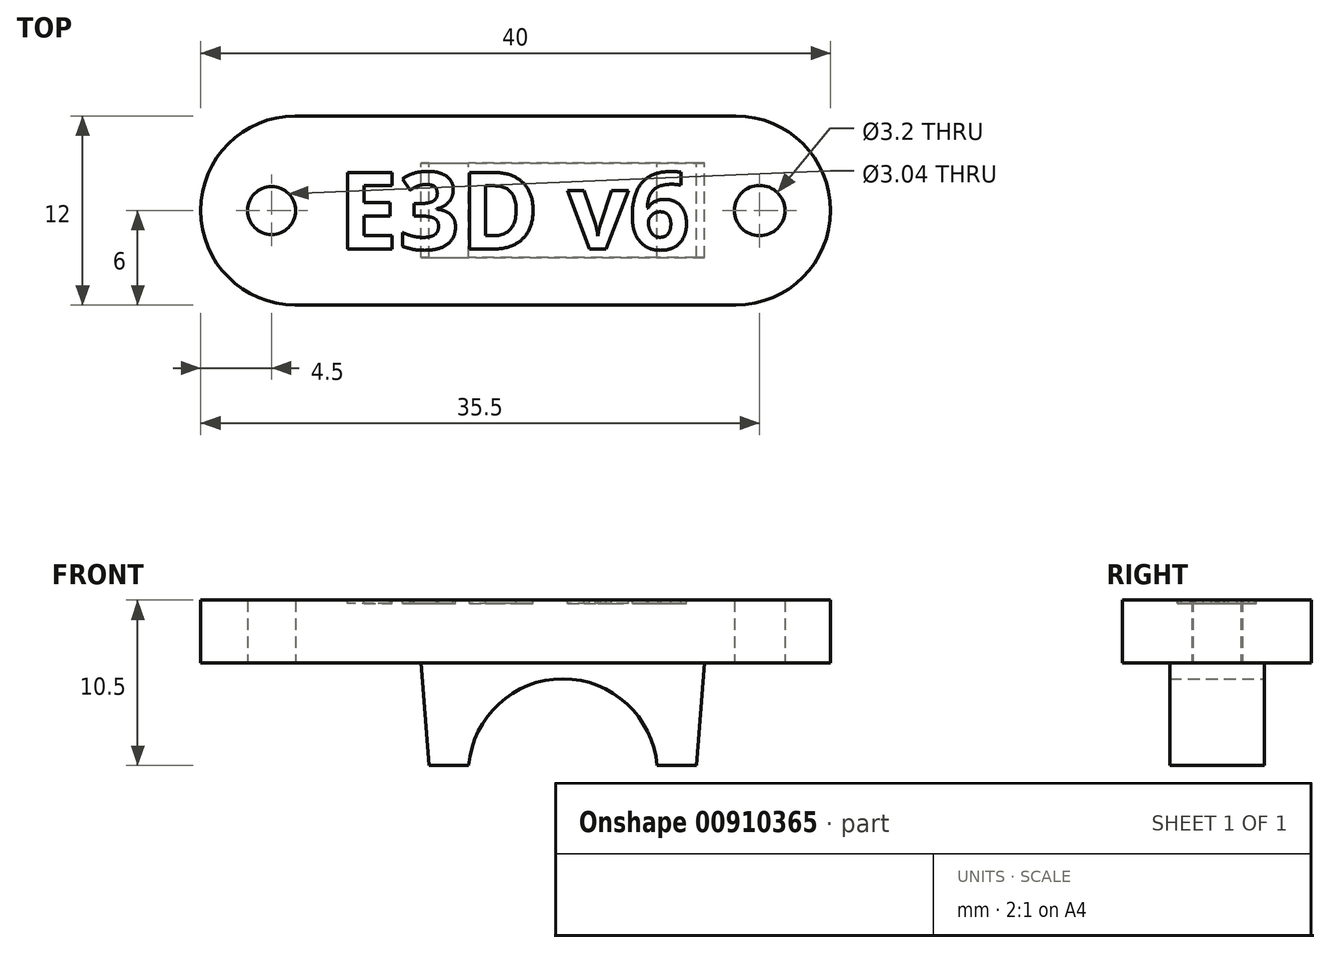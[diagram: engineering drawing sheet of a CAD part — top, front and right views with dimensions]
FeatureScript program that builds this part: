
annotation { "Feature Type Name" : "Feature", "Feature Type Description" : "" }
export const myFeature = defineFeature(function(context is Context, id is Id, definition is map)
    precondition{}
    {
        {
            var Q0;
            Q0=qCreatedBy(makeId("Top.planeOp"),FACE);
            var sketch = newSketch(context, id + "F0", { "sketchPlane" : qUnion([Q0])});
            skLineSegment(sketch, "E0.bottom", {"start": v(20, 6) * mm, "end": v(-20, 6) * mm});
            skLineSegment(sketch, "E0.top", {"start": v(20, -6) * mm, "end": v(-20, -6) * mm});
            skLineSegment(sketch, "E0.left", {"start": v(20, 6) * mm, "end": v(20, -6) * mm});
            skLineSegment(sketch, "E0.right", {"start": v(-20, 6) * mm, "end": v(-20, -6) * mm});
            skPoint(sketch, "E0.middle", {"position": v(0, 0) * mm});
            skCircle(sketch, "E1", {"center": v(15.5, 0) * mm, "radius": 1.6 * mm});
            skCircle(sketch, "E2", {"center": v(-15.5, 0) * mm, "radius": 1.52 * mm});
            skLineSegment(sketch, "E3", {"start": v(-15.5, 0) * mm, "end": v(15.5, 0) * mm, "construction": true});
            skSolve(sketch);
        }
        {
            var Q0;
            Q0 = qSketchRegion(id + "F0", true);
            extrude(context, id + "F1", {"entities" : qUnion([Q0]), "depth" : 4 * mm, "offsetDistance" : 25.4 * mm});
        }
        {
            var Q0;
            Q0=qCreatedBy(makeId("Front.planeOp"),FACE);
            var sketch = newSketch(context, id + "F2", { "sketchPlane" : qUnion([Q0])});
            skLineSegment(sketch, "E4", {"start": v(-5.5, -6.5) * mm, "end": v(-6, 0) * mm});
            skLineSegment(sketch, "E5", {"start": v(-6, 0) * mm, "end": v(12, 0) * mm});
            skLineSegment(sketch, "E6", {"start": v(12, 0) * mm, "end": v(11.5, -6.5) * mm});
            skLineSegment(sketch, "E7", {"start": v(11.5, -6.5) * mm, "end": v(8.98, -6.5) * mm});
            skLineSegment(sketch, "E8", {"start": v(-5.5, -6.5) * mm, "end": v(-2.98, -6.5) * mm});
            skArc(sketch, "E9", {"start": v(8.98, -6.5) * mm, "mid": v(3, -1) * mm, "end": v(-2.98, -6.5) * mm});
            skSolve(sketch);
        }
        {
            var Q0;
            Q0 = qSketchRegion(id + "F2", true);
            extrude(context, id + "F3", {"entities" : qUnion([Q0]), "operationType" : NewBodyOperationType.ADD, "depth" : 6 * mm, "offsetDistance" : 25.4 * mm, "symmetric" : true});
        }
        {
            var Q0;
            Q0=makeQuery(id+"F1.opExtrude","SWEPT_EDGE",EDGE,{"disambiguationData":[OSD([sQuery(id+"F0.wireOp",EDGE,"E0.bottom"),sQuery(id+"F0.wireOp",EDGE,"E0.left")])]});
            var Q1;
            Q1=makeQuery(id+"F1.opExtrude","SWEPT_EDGE",EDGE,{"disambiguationData":[OSD([sQuery(id+"F0.wireOp",EDGE,"E0.top"),sQuery(id+"F0.wireOp",EDGE,"E0.left")])]});
            var Q2;
            Q2=makeQuery(id+"F1.opExtrude","SWEPT_EDGE",EDGE,{"disambiguationData":[OSD([sQuery(id+"F0.wireOp",EDGE,"E0.top"),sQuery(id+"F0.wireOp",EDGE,"E0.right")])]});
            var Q3;
            Q3=makeQuery(id+"F1.opExtrude","SWEPT_EDGE",EDGE,{"disambiguationData":[OSD([sQuery(id+"F0.wireOp",EDGE,"E0.bottom"),sQuery(id+"F0.wireOp",EDGE,"E0.right")])]});
            fillet(context, id + "F4", {"entities" : qUnion([Q0, Q1, Q2, Q3]), "radius" : 6 * mm, "tangentPropagation" : true, "allowEdgeOverflow" : false});
        }
        {
            var Q0;
            Q0=makeQuery(id+"F1.opExtrude","CAP_FACE",FACE,{"disambiguationData":[OSD([sQuery(id+"F0.wireOp",EDGE,"E0.bottom"),sQuery(id+"F0.wireOp",EDGE,"E0.top"),sQuery(id+"F0.wireOp",EDGE,"E0.left"),sQuery(id+"F0.wireOp",EDGE,"E0.right"),sQuery(id+"F0.wireOp",EDGE,"E1"),sQuery(id+"F0.wireOp",EDGE,"E2")])],"isStart":false});
            var sketch = newSketch(context, id + "F5", { "sketchPlane" : qUnion([Q0])});
            skText(sketch, "E10", { "text": "E3D v6", "fontName": "OpenSans-Bold.ttf"});
            const initialGuessF5  = {"E10": [-0.01128, -0.00246, 1, 0, 0.00492]};
            skSetInitialGuess(sketch, initialGuessF5);
            skSolve(sketch);
        }
        {
            var Q0;
            Q0 = qSketchRegion(id + "F5", true);
            extrude(context, id + "F6", {"entities" : qUnion([Q0]), "operationType" : NewBodyOperationType.REMOVE, "oppositeDirection" : true, "depth" : .2 * mm, "offsetDistance" : 25.4 * mm});
        }
    });
